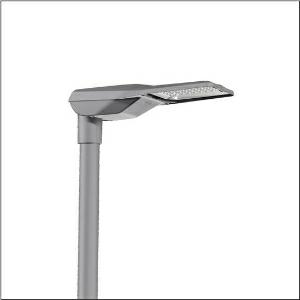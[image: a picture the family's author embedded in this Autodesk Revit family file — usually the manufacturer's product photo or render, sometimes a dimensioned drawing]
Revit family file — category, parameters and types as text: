
# Revit family: streetlight_sl_21_iq_mini___pl52_5xe2h31g08hb_1606
name_source: partatom
category: Lighting Fixtures
units: mm (PartAtom-declared; Revit-internal decimal feet)

## family parameters
Cut with Voids When Loaded = No
Host = Face
Light Source = No
Part Type = Normal
Room Calculation Point = No
Round Connector Dimension = Use Diameter
Shared = No

## types (1)
- --- (1 x LED, 9290 lm, 70.9 W, 3000K)
    Apparent Load = 71 VA
    CIE Flux Codes = 27 59 98 100 100
    Color Rendering = 70
    Color Temperature = 3000K
    Default Elevation = 1800 mm
    Description = Streetlight SL 21 iQ mini, mast luminaire, primary light control with lens, of PMMA, primary optical cover: cover, of toughened safety glass, transparent, light distribution: PL52, light emission: direct distribution, primary light characteristic: asymmetric, installation type: post-top, side-entry, LED, High Power LED, rated luminous flux: 9.290lm, luminous efficacy: 131lm/W, light colour: 730, colour temperature: 3000K, control gear: iQ Street-Remote, control: Street-Remote, Auto-Match, Temp-Guard, Lumen-Switch, Night-Set, Smart-Wire, Light-Fading, Desk-Remote (wireless, voltage-free reading and setting of iQ features in the workshop via application-optimized NFC function/RFID function), optimised constant luminous flux control (CLO 2.0), pre-setting: linear dimming characteristic, mains connection: 220..240V, AC, 50/60Hz, start of lifetime: 71W, end of service life: 75W, reduction: 31W, luminaire housing, of diecast aluminium, powder-coated, Siteco® metallic grey (DB 702S), corrosivity category C5 mid according to DIN EN ISO 12944, please order mast flange separately, inclination adjustable: 0°, 5°, 10°, 15°, sealing non-destructively replaceable, multi-level sealing system, length: 628mm, width: 235mm, height: 110mm, mast flange for spigot size: 42mm (side-entry): 5XC10008XM4, 60/48mm (side-entry/post-top): 5XC10108XM2, 76/60mm (side-entry/post-top): 5XC10108XM1, mounting height: 4..8m, protection rating (complete): IP66, insulation class (complete): insulation class II (safety insulation), certification: CE, ENEC, ENEC+, VDE, impact resistance: IK10, permissible operating ambient temperature for outdoor applications: -40..+50°C, standard-compliant lighting for roads and squares, packaging unit: 1 piece

Light Distribution: PL52
    Height = 110 mm
    Lamp = 1 x LED
    Lamp Light Flux = 9290 lm
    Lamp Power = 70.9 W
    Lamp count = 1
    Length = 625 mm
    Luminous efficacy = 131 lm/W
    Manufacturer = Siteco
    ModVariant = No
    Model = 5XE2H31G08HB
    Number of Poles = 1
    OnlyDefault = Yes
    Power Factor = 1
    Product Name = Streetlight SL 21 iQ mini | PL52
    Product group = mast luminaire | pylon top
    ProductGroupID = 6100
    Protection Class = Protection class II
    Protection Degree = IP 66
    RLX_Detail_Level = 1
    RLX_Emergency_Light_Flux = 0 lm
    RLX_Emergency_Type = 0
    RLX_Emergency_Type_DB = No
    RlxData = <blob elided: 35945 chars, md5=eb47581f>
    Socket = socket
    Standby Power = 0 W
    System Light Flux = 9290 lm
    System Power = 71 W
    Type Comments = factory setting: luminous flux: 100 % | dim-lin: 254 | 711 mA
    Type Image = l_1003519.jpg
    URL = http://relux.com
    VarID = @adj_179895
    Voltage = 0 V
    Weight = 0.00 kg
    Width = 234 mm

## geometry (parser evidence)
native form markers: Blend x4, Sweep x11
no freeform markers — native parametric forms only
